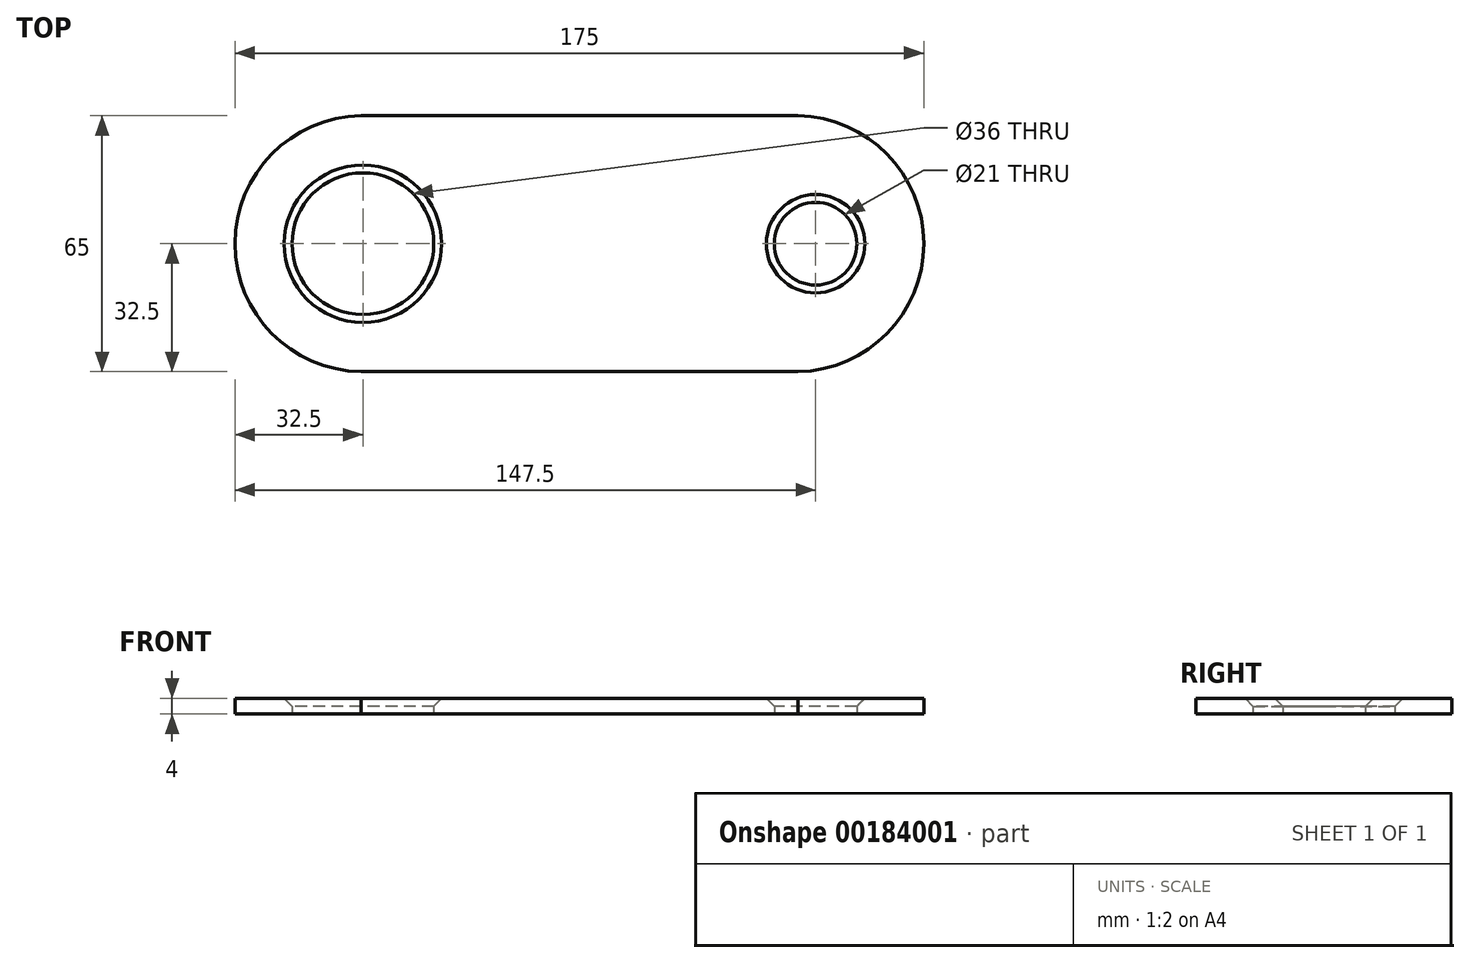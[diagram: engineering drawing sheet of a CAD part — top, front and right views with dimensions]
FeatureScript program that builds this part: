
annotation { "Feature Type Name" : "Feature", "Feature Type Description" : "" }
export const myFeature = defineFeature(function(context is Context, id is Id, definition is map)
    precondition{}
    {
        {
            var Q0;
            Q0=qCreatedBy(makeId("Top.planeOp"),FACE);
            var sketch = newSketch(context, id + "F0", { "sketchPlane" : qUnion([Q0])});
            skLineSegment(sketch, "E0.bottom", {"start": v(-55.5, -32.5) * mm, "end": v(55.5, -32.5) * mm});
            skLineSegment(sketch, "E0.top", {"start": v(-55.5, 32.5) * mm, "end": v(55.5, 32.5) * mm});
            skLineSegment(sketch, "E0.left", {"start": v(-55.5, -32.5) * mm, "end": v(-55.5, 32.5) * mm, "construction": true});
            skLineSegment(sketch, "E0.right", {"start": v(55.5, -32.5) * mm, "end": v(55.5, 32.5) * mm, "construction": true});
            skPoint(sketch, "E0.middle", {"position": v(0, 0) * mm});
            skLineSegment(sketch, "E1", {"start": v(0, 0) * mm, "end": v(-87.5, 0) * mm, "construction": true});
            skPoint(sketch, "E1.endSnap0", {"position": v(-55.5, 0) * mm});
            skLineSegment(sketch, "E2", {"start": v(0, 0) * mm, "end": v(87.5, 0) * mm, "construction": true});
            skArc(sketch, "E3", {"start": v(-55.5, 32.5) * mm, "mid": v(-87.5, 0) * mm, "end": v(-55.5, -32.5) * mm});
            skArc(sketch, "E4", {"start": v(55.5, -32.5) * mm, "mid": v(87.5, 0) * mm, "end": v(55.5, 32.5) * mm});
            skCircle(sketch, "E5", {"center": v(-55, 0) * mm, "radius": 18 * mm});
            skCircle(sketch, "E6", {"center": v(60, 0) * mm, "radius": 10.5 * mm});
            skSolve(sketch);
        }
        {
            var Q0;
            Q0=makeQuery(id+"F0.imprint","IMPRINT",FACE,{"disambiguationData":[TD([[makeQuery(id+"F0.imprint","IMPRINT",EDGE,{"derivedFrom":sQuery(id+"F0.wireOp",EDGE,"E0.bottom")}),1.0]])]});
            extrude(context, id + "F1", {"entities" : qUnion([Q0]), "depth" : 4 * mm});
        }
        {
            var Q0;
            Q0=makeQuery(id+"F1.opExtrude","CAP_EDGE",EDGE,{"disambiguationData":[OSD([sQuery(id+"F0.wireOp",EDGE,"E5")])],"isStart":false});
            var Q1;
            Q1=makeQuery(id+"F1.opExtrude","CAP_EDGE",EDGE,{"disambiguationData":[OSD([sQuery(id+"F0.wireOp",EDGE,"n59XOhcH-MVG2-5y0t-HSSG-ehqfXdBhbJFc")])],"isStart":false});
            var Q2;
            Q2=makeQuery(id+"F1.opExtrude","CAP_EDGE",EDGE,{"disambiguationData":[OSD([sQuery(id+"F0.wireOp",EDGE,"E6")])],"isStart":false});
            chamfer(context, id + "F2", {"entities" : qUnion([Q0, Q1, Q2]), "width" : 2 * mm, "tangentPropagation" : true});
        }
    });
